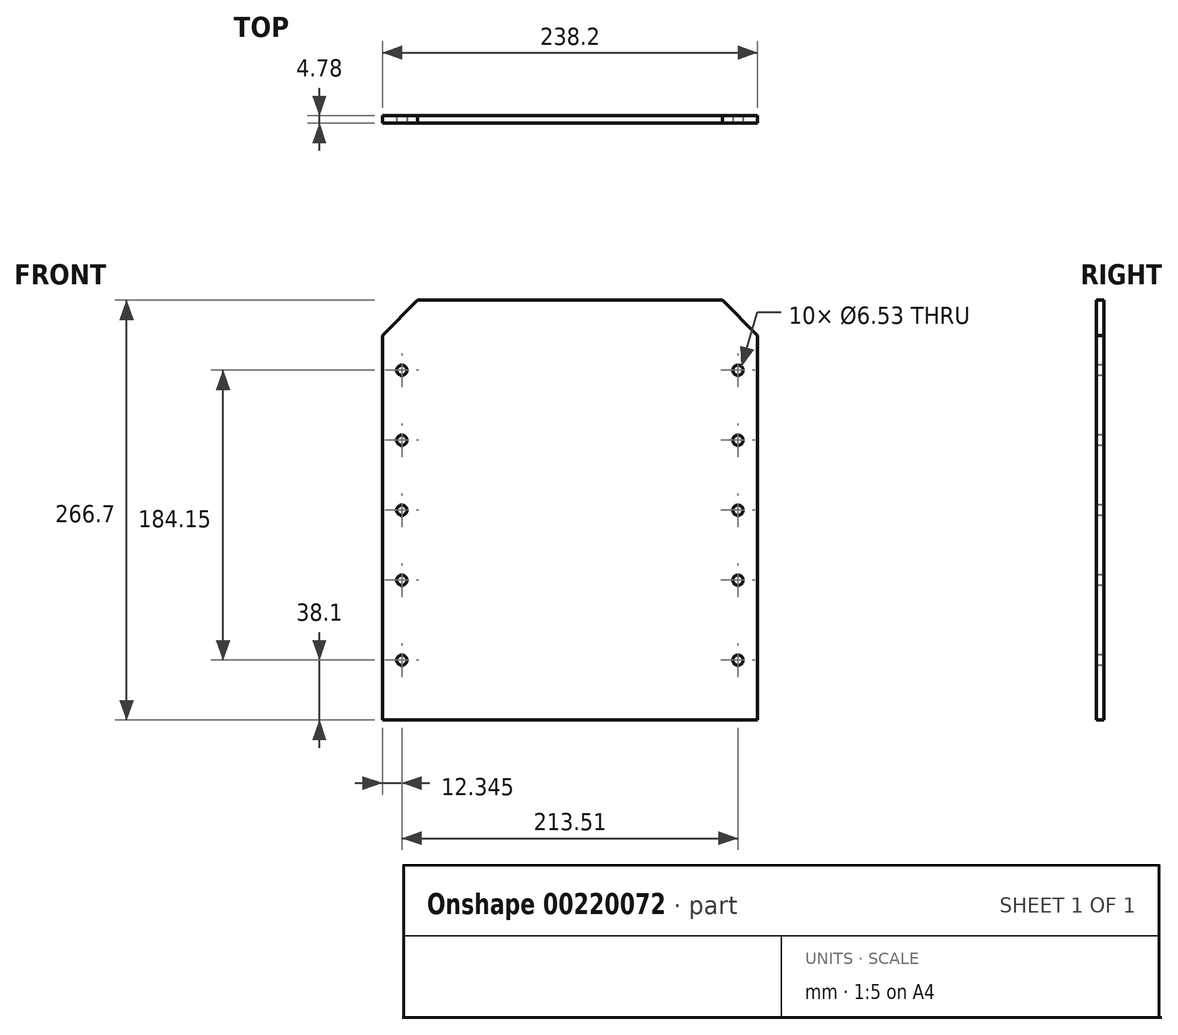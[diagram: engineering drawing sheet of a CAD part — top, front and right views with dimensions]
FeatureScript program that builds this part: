
annotation { "Feature Type Name" : "Feature", "Feature Type Description" : "" }
export const myFeature = defineFeature(function(context is Context, id is Id, definition is map)
    precondition{}
    {
        {
            var Q0;
            Q0=qCreatedBy(makeId("Front.planeOp"),FACE);
            var sketch = newSketch(context, id + "F0", { "sketchPlane" : qUnion([Q0])});
            skLineSegment(sketch, "E0.bottom", {"start": v(119.1, 133.35) * mm, "end": v(-119.1, 133.35) * mm});
            skLineSegment(sketch, "E0.top", {"start": v(119.1, -133.35) * mm, "end": v(-119.1, -133.35) * mm});
            skLineSegment(sketch, "E0.left", {"start": v(119.1, 133.35) * mm, "end": v(119.1, -133.35) * mm});
            skLineSegment(sketch, "E0.right", {"start": v(-119.1, 133.35) * mm, "end": v(-119.1, -133.35) * mm});
            skPoint(sketch, "E0.middle", {"position": v(0, 0) * mm});
            skLineSegment(sketch, "E1", {"start": v(-106.75, 141.4) * mm, "end": v(-106.75, -152.08) * mm, "construction": true});
            skCircle(sketch, "E2", {"center": v(-106.75, 88.9) * mm, "radius": 3.26 * mm});
            skCircle(sketch, "E3", {"center": v(-106.75, 44.45) * mm, "radius": 3.26 * mm});
            skCircle(sketch, "E4", {"center": v(-106.75, 0) * mm, "radius": 3.26 * mm});
            skCircle(sketch, "E5", {"center": v(-106.75, -44.45) * mm, "radius": 3.26 * mm});
            skCircle(sketch, "E6.MirrorC", {"center": v(106.75, -44.45) * mm, "radius": 3.26 * mm});
            skCircle(sketch, "E7.MirrorC", {"center": v(106.75, 88.9) * mm, "radius": 3.26 * mm});
            skCircle(sketch, "E8.MirrorC", {"center": v(106.75, 44.45) * mm, "radius": 3.26 * mm});
            skCircle(sketch, "E9.MirrorC", {"center": v(106.75, 0) * mm, "radius": 3.26 * mm});
            skCircle(sketch, "E10", {"center": v(-106.75, -95.25) * mm, "radius": 3.26 * mm});
            skCircle(sketch, "E11.MirrorC", {"center": v(106.75, -95.25) * mm, "radius": 3.26 * mm});
            skSolve(sketch);
        }
        {
            var Q0;
            Q0 = qSketchRegion(id + "F0", true);
            extrude(context, id + "F1", {"entities" : qUnion([Q0]), "oppositeDirection" : true, "depth" : 4.78 * mm});
        }
        {
            var Q0;
            Q0=makeQuery(id+"F1.opExtrude","SWEPT_EDGE",EDGE,{"disambiguationData":[OSD([sQuery(id+"F0.wireOp",EDGE,"E0.bottom"),sQuery(id+"F0.wireOp",EDGE,"E0.left")])]});
            var Q1;
            Q1=makeQuery(id+"F1.opExtrude","SWEPT_EDGE",EDGE,{"disambiguationData":[OSD([sQuery(id+"F0.wireOp",EDGE,"E0.bottom"),sQuery(id+"F0.wireOp",EDGE,"E0.right")])]});
            chamfer(context, id + "F2", {"entities" : qUnion([Q0, Q1]), "width" : 22.35 * mm, "tangentPropagation" : true});
        }
    });
